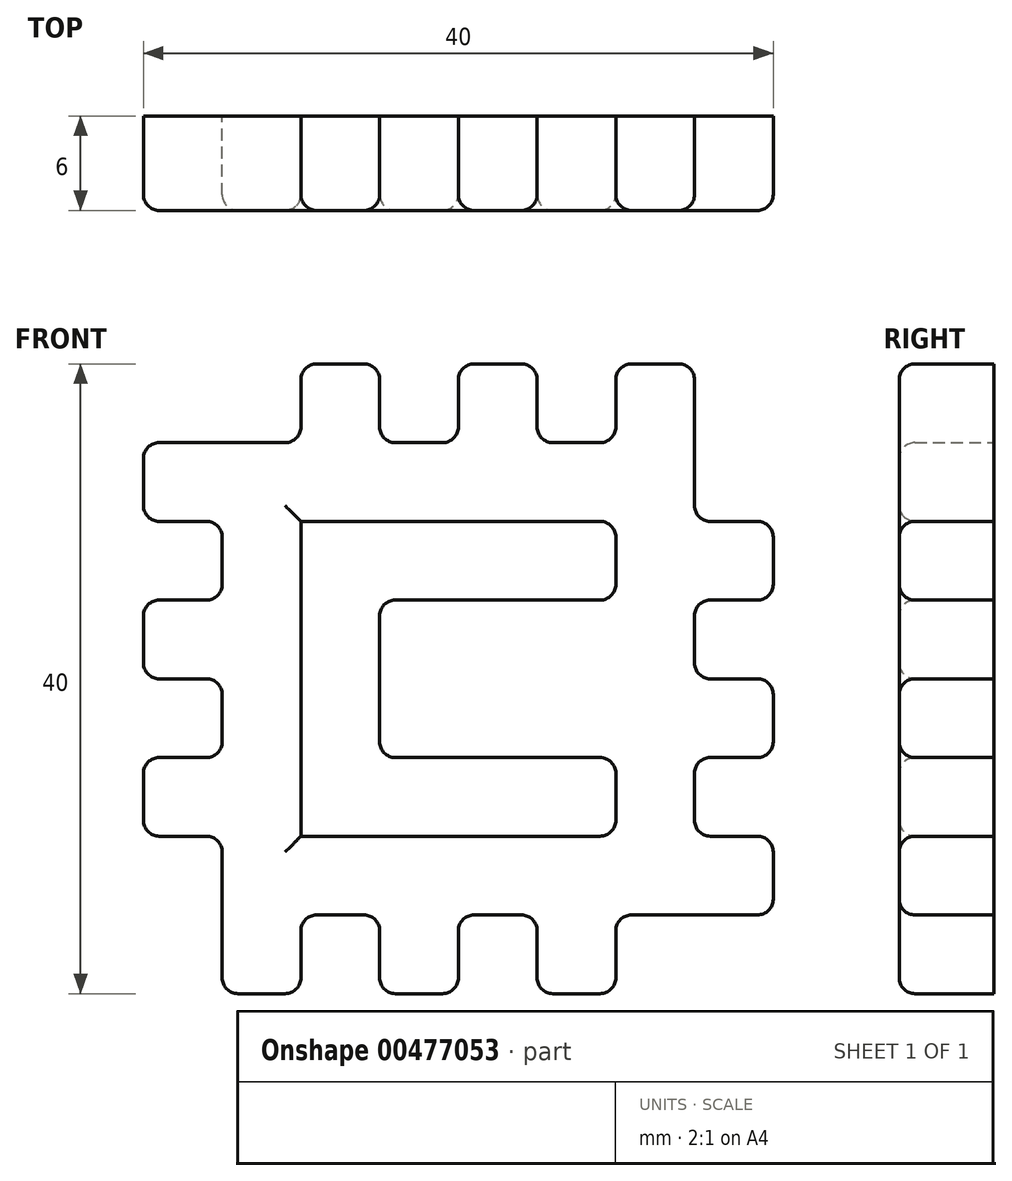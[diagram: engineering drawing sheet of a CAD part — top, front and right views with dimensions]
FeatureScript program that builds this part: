
annotation { "Feature Type Name" : "Feature", "Feature Type Description" : "" }
export const myFeature = defineFeature(function(context is Context, id is Id, definition is map)
    precondition{}
    {
        {
            var Q0;
            Q0=qCreatedBy(makeId("Front.planeOp"),FACE);
            var sketch = newSketch(context, id + "F0", { "sketchPlane" : qUnion([Q0])});
            skLineSegment(sketch, "E0.bottom", {"start": v(-15, -15) * mm, "end": v(15, -15) * mm});
            skLineSegment(sketch, "E0.top", {"start": v(-15, 15) * mm, "end": v(15, 15) * mm});
            skLineSegment(sketch, "E0.left", {"start": v(-15, -15) * mm, "end": v(-15, 15) * mm});
            skLineSegment(sketch, "E0.right", {"start": v(15, -15) * mm, "end": v(15, 15) * mm});
            skPoint(sketch, "E0.middle", {"position": v(0, 0) * mm});
            skLineSegment(sketch, "E1.bottom", {"start": v(-15, 15) * mm, "end": v(-20, 15) * mm});
            skLineSegment(sketch, "E1.top", {"start": v(-15, 10) * mm, "end": v(-20, 10) * mm});
            skLineSegment(sketch, "E1.left", {"start": v(-15, 15) * mm, "end": v(-15, 10) * mm});
            skLineSegment(sketch, "E1.right", {"start": v(-20, 15) * mm, "end": v(-20, 10) * mm});
            skPoint(sketch, "E2", {"position": v(-15, 0) * mm});
            skPoint(sketch, "E3", {"position": v(0, 15) * mm});
            skPoint(sketch, "E4", {"position": v(15, 0) * mm});
            skPoint(sketch, "E5", {"position": v(0, -15) * mm});
            skLineSegment(sketch, "E6.bottom", {"start": v(-15, 0) * mm, "end": v(-20, 0) * mm});
            skLineSegment(sketch, "E6.top", {"start": v(-15, 5) * mm, "end": v(-20, 5) * mm});
            skLineSegment(sketch, "E6.left", {"start": v(-15, 0) * mm, "end": v(-15, 5) * mm});
            skLineSegment(sketch, "E6.right", {"start": v(-20, 0) * mm, "end": v(-20, 5) * mm});
            skPoint(sketch, "E7", {"position": v(-15, -7.74) * mm});
            skPoint(sketch, "E8", {"position": v(-7.28, -15) * mm});
            skPoint(sketch, "E9", {"position": v(7.64, -15) * mm});
            skPoint(sketch, "E10", {"position": v(15, -7.4) * mm});
            skPoint(sketch, "E11", {"position": v(15, 8.08) * mm});
            skPoint(sketch, "E12", {"position": v(7.83, 15) * mm});
            skPoint(sketch, "E13", {"position": v(-7.7, 15) * mm});
            skPoint(sketch, "E14", {"position": v(-15, -5) * mm});
            skPoint(sketch, "E15", {"position": v(-15, -11.17) * mm});
            skPoint(sketch, "E16", {"position": v(-11.04, -15) * mm});
            skPoint(sketch, "E17", {"position": v(-3.27, -15) * mm});
            skPoint(sketch, "E18", {"position": v(5, -15) * mm});
            skPoint(sketch, "E19", {"position": v(11.4, -15) * mm});
            skPoint(sketch, "E20", {"position": v(15, -11.1) * mm});
            skPoint(sketch, "E21", {"position": v(15, -3.78) * mm});
            skPoint(sketch, "E22", {"position": v(15, 3.83) * mm});
            skPoint(sketch, "E23", {"position": v(15, 10) * mm});
            skPoint(sketch, "E24", {"position": v(11.09, 15) * mm});
            skPoint(sketch, "E25", {"position": v(4.04, 15) * mm});
            skPoint(sketch, "E26", {"position": v(-3.6, 15) * mm});
            skPoint(sketch, "E27", {"position": v(-11.54, 15) * mm});
            skLineSegment(sketch, "E28.bottom", {"start": v(-15, -5) * mm, "end": v(-20, -5) * mm});
            skLineSegment(sketch, "E28.top", {"start": v(-15, -10) * mm, "end": v(-20, -10) * mm});
            skLineSegment(sketch, "E28.left", {"start": v(-15, -5) * mm, "end": v(-15, -10) * mm});
            skLineSegment(sketch, "E28.right", {"start": v(-20, -5) * mm, "end": v(-20, -10) * mm});
            skLineSegment(sketch, "E29.bottom", {"start": v(15, 10) * mm, "end": v(20, 10) * mm});
            skLineSegment(sketch, "E29.top", {"start": v(15, 5) * mm, "end": v(20, 5) * mm});
            skLineSegment(sketch, "E29.left", {"start": v(15, 10) * mm, "end": v(15, 5) * mm});
            skLineSegment(sketch, "E29.right", {"start": v(20, 10) * mm, "end": v(20, 5) * mm});
            skLineSegment(sketch, "E30.bottom", {"start": v(15, 0) * mm, "end": v(20, 0) * mm});
            skLineSegment(sketch, "E30.top", {"start": v(15, -5) * mm, "end": v(20, -5) * mm});
            skLineSegment(sketch, "E30.left", {"start": v(15, 0) * mm, "end": v(15, -5) * mm});
            skLineSegment(sketch, "E30.right", {"start": v(20, 0) * mm, "end": v(20, -5) * mm});
            skLineSegment(sketch, "E31.bottom", {"start": v(15, -15) * mm, "end": v(20, -15) * mm});
            skLineSegment(sketch, "E31.top", {"start": v(15, -10) * mm, "end": v(20, -10) * mm});
            skLineSegment(sketch, "E31.left", {"start": v(15, -15) * mm, "end": v(15, -10) * mm});
            skLineSegment(sketch, "E31.right", {"start": v(20, -15) * mm, "end": v(20, -10) * mm});
            skLineSegment(sketch, "E32.bottom", {"start": v(-15, -15) * mm, "end": v(-10, -15) * mm});
            skLineSegment(sketch, "E32.top", {"start": v(-15, -20) * mm, "end": v(-10, -20) * mm});
            skLineSegment(sketch, "E32.left", {"start": v(-15, -15) * mm, "end": v(-15, -20) * mm});
            skLineSegment(sketch, "E32.right", {"start": v(-10, -15) * mm, "end": v(-10, -20) * mm});
            skLineSegment(sketch, "E33.bottom", {"start": v(0, -15) * mm, "end": v(-5, -15) * mm});
            skLineSegment(sketch, "E33.top", {"start": v(0, -20) * mm, "end": v(-5, -20) * mm});
            skLineSegment(sketch, "E33.left", {"start": v(0, -15) * mm, "end": v(0, -20) * mm});
            skLineSegment(sketch, "E33.right", {"start": v(-5, -15) * mm, "end": v(-5, -20) * mm});
            skLineSegment(sketch, "E34.bottom", {"start": v(5, -15) * mm, "end": v(10, -15) * mm});
            skLineSegment(sketch, "E34.top", {"start": v(5, -20) * mm, "end": v(10, -20) * mm});
            skLineSegment(sketch, "E34.left", {"start": v(5, -15) * mm, "end": v(5, -20) * mm});
            skLineSegment(sketch, "E34.right", {"start": v(10, -15) * mm, "end": v(10, -20) * mm});
            skLineSegment(sketch, "E35.bottom", {"start": v(-10, 15) * mm, "end": v(-5, 15) * mm});
            skLineSegment(sketch, "E35.top", {"start": v(-10, 20) * mm, "end": v(-5, 20) * mm});
            skLineSegment(sketch, "E35.left", {"start": v(-10, 15) * mm, "end": v(-10, 20) * mm});
            skLineSegment(sketch, "E35.right", {"start": v(-5, 15) * mm, "end": v(-5, 20) * mm});
            skLineSegment(sketch, "E36.bottom", {"start": v(0, 15) * mm, "end": v(5, 15) * mm});
            skLineSegment(sketch, "E36.top", {"start": v(0, 20) * mm, "end": v(5, 20) * mm});
            skLineSegment(sketch, "E36.left", {"start": v(0, 15) * mm, "end": v(0, 20) * mm});
            skLineSegment(sketch, "E36.right", {"start": v(5, 15) * mm, "end": v(5, 20) * mm});
            skLineSegment(sketch, "E37.bottom", {"start": v(15, 15) * mm, "end": v(10, 15) * mm});
            skLineSegment(sketch, "E37.top", {"start": v(15, 20) * mm, "end": v(10, 20) * mm});
            skLineSegment(sketch, "E37.left", {"start": v(15, 15) * mm, "end": v(15, 20) * mm});
            skLineSegment(sketch, "E37.right", {"start": v(10, 15) * mm, "end": v(10, 20) * mm});
            skLineSegment(sketch, "E38.bottom", {"start": v(10, 10) * mm, "end": v(-10, 10) * mm});
            skLineSegment(sketch, "E38.top", {"start": v(10, 5) * mm, "end": v(-10, 5) * mm});
            skLineSegment(sketch, "E38.left", {"start": v(10, 10) * mm, "end": v(10, 5) * mm});
            skLineSegment(sketch, "E38.right", {"start": v(-10, 10) * mm, "end": v(-10, 5) * mm});
            skLineSegment(sketch, "E39.bottom", {"start": v(10, -5) * mm, "end": v(-10, -5) * mm});
            skLineSegment(sketch, "E39.top", {"start": v(10, -10) * mm, "end": v(-10, -10) * mm});
            skLineSegment(sketch, "E39.left", {"start": v(10, -5) * mm, "end": v(10, -10) * mm});
            skLineSegment(sketch, "E39.right", {"start": v(-10, -5) * mm, "end": v(-10, -10) * mm});
            skLineSegment(sketch, "E40.bottom", {"start": v(-5, 10) * mm, "end": v(-10, 10) * mm});
            skLineSegment(sketch, "E40.top", {"start": v(-5, -10) * mm, "end": v(-10, -10) * mm});
            skLineSegment(sketch, "E40.left", {"start": v(-5, 10) * mm, "end": v(-5, -10) * mm});
            skLineSegment(sketch, "E40.right", {"start": v(-10, 10) * mm, "end": v(-10, -10) * mm});
            skSolve(sketch);
        }
        {
            var Q0;
            Q0 = qSketchRegion(id + "F0", true);
            extrude(context, id + "F1", {"entities" : qUnion([Q0]), "depth" : 6 * mm});
        }
        {
            var Q0;
            Q0=makeQuery(id+"F1.opExtrude","SWEPT_EDGE",EDGE,{"disambiguationData":[OSD([sQuery(id+"F0.wireOp",EDGE,"E40.bottom"),sQuery(id+"F0.wireOp",EDGE,"E40.right")])]});
            var Q1;
            Q1=makeQuery(id+"F1.opExtrude","SWEPT_EDGE",EDGE,{"disambiguationData":[OSD([sQuery(id+"F0.wireOp",EDGE,"E39.bottom"),sQuery(id+"F0.wireOp",EDGE,"E40.left")])]});
            var Q2;
            Q2=makeQuery(id+"F1.opExtrude","SWEPT_EDGE",EDGE,{"disambiguationData":[OSD([sQuery(id+"F0.wireOp",EDGE,"E38.bottom"),sQuery(id+"F0.wireOp",EDGE,"E38.left")])]});
            var Q3;
            Q3=makeQuery(id+"F1.opExtrude","SWEPT_EDGE",EDGE,{"disambiguationData":[OSD([sQuery(id+"F0.wireOp",EDGE,"E39.bottom"),sQuery(id+"F0.wireOp",EDGE,"E39.left")])]});
            var Q4;
            Q4=makeQuery(id+"F1.opExtrude","SWEPT_EDGE",EDGE,{"disambiguationData":[OSD([sQuery(id+"F0.wireOp",EDGE,"E38.top"),sQuery(id+"F0.wireOp",EDGE,"E38.left")])]});
            var Q5;
            Q5=makeQuery(id+"F1.opExtrude","SWEPT_EDGE",EDGE,{"disambiguationData":[OSD([sQuery(id+"F0.wireOp",EDGE,"E39.top"),sQuery(id+"F0.wireOp",EDGE,"E39.left")])]});
            var Q6;
            Q6=makeQuery(id+"F1.opExtrude","SWEPT_EDGE",EDGE,{"disambiguationData":[OSD([sQuery(id+"F0.wireOp",EDGE,"E38.top"),sQuery(id+"F0.wireOp",EDGE,"E40.left")])]});
            var Q7;
            Q7=makeQuery(id+"F1.opExtrude","SWEPT_EDGE",EDGE,{"disambiguationData":[OSD([sQuery(id+"F0.wireOp",EDGE,"E40.top"),sQuery(id+"F0.wireOp",EDGE,"E40.right")])]});
            var Q8;
            Q8=makeQuery(id+"F1.opExtrude","CAP_EDGE",EDGE,{"disambiguationData":[OSD([sQuery(id+"F0.wireOp",EDGE,"E39.bottom")])],"isStart":false});
            var Q9;
            Q9=makeQuery(id+"F1.opExtrude","CAP_EDGE",EDGE,{"disambiguationData":[OSD([sQuery(id+"F0.wireOp",EDGE,"E40.left")])],"isStart":false});
            fillet(context, id + "F2", {"entities" : qUnion([Q0, Q1, Q2, Q3, Q4, Q5, Q6, Q7, Q8, Q9]), "radius" : 1 * mm, "tangentPropagation" : true, "allowEdgeOverflow" : false});
        }
        {
            var Q0;
            Q0=makeQuery(id+"F1.opExtrude","CAP_EDGE",EDGE,{"disambiguationData":[OSD([sQuery(id+"F0.wireOp",EDGE,"E35.right")])],"isStart":false});
            var Q1;
            {var subQ0=sQuery(id+"F0.wireOp",EDGE,"E0.top");Q1=makeQuery(id+"F1.opExtrude","CAP_EDGE",EDGE,{"disambiguationData":[OSD([subQ0]),TDD([makeQuery(id+"F0.imprint","IMPRINT",EDGE,{"disambiguationData":[TD([[makeQuery(id+"F0.imprint","INTERSECT",VERTEX,{"derivedFrom":[subQ0,sQuery(id+"F0.wireOp",EDGE,"E35.bottom"),sQuery(id+"F0.wireOp",EDGE,"E35.right")]}),-1.0]])],"derivedFrom":subQ0})])],"isStart":false});}
            var Q2;
            {var subQ0=sQuery(id+"F0.wireOp",EDGE,"E0.top");Q2=makeQuery(id+"F1.opExtrude","CAP_EDGE",EDGE,{"disambiguationData":[OSD([subQ0]),TDD([makeQuery(id+"F0.imprint","IMPRINT",EDGE,{"disambiguationData":[TD([[makeQuery(id+"F0.imprint","INTERSECT",VERTEX,{"derivedFrom":[subQ0,sQuery(id+"F0.wireOp",EDGE,"E37.bottom"),sQuery(id+"F0.wireOp",EDGE,"E37.right")]}),1.0]])],"derivedFrom":subQ0})])],"isStart":false});}
            var Q3;
            Q3=makeQuery(id+"F1.opExtrude","CAP_EDGE",EDGE,{"disambiguationData":[OSD([sQuery(id+"F0.wireOp",EDGE,"E36.right")])],"isStart":false});
            var Q4;
            Q4=makeQuery(id+"F1.opExtrude","SWEPT_EDGE",EDGE,{"disambiguationData":[OSD([sQuery(id+"F0.wireOp",EDGE,"E0.top"),sQuery(id+"F0.wireOp",EDGE,"E37.bottom"),sQuery(id+"F0.wireOp",EDGE,"E37.right")])]});
            var Q5;
            Q5=makeQuery(id+"F1.opExtrude","SWEPT_EDGE",EDGE,{"disambiguationData":[OSD([sQuery(id+"F0.wireOp",EDGE,"E0.top"),sQuery(id+"F0.wireOp",EDGE,"E36.bottom"),sQuery(id+"F0.wireOp",EDGE,"E36.left")])]});
            var Q6;
            Q6=makeQuery(id+"F1.opExtrude","CAP_EDGE",EDGE,{"disambiguationData":[OSD([sQuery(id+"F0.wireOp",EDGE,"E0.top"),sQuery(id+"F0.wireOp",EDGE,"E1.bottom")])],"isStart":false});
            var Q7;
            Q7=makeQuery(id+"F1.opExtrude","SWEPT_EDGE",EDGE,{"disambiguationData":[OSD([sQuery(id+"F0.wireOp",EDGE,"E0.top"),sQuery(id+"F0.wireOp",EDGE,"E35.bottom"),sQuery(id+"F0.wireOp",EDGE,"E35.left")])]});
            var Q8;
            Q8=makeQuery(id+"F1.opExtrude","CAP_EDGE",EDGE,{"disambiguationData":[OSD([sQuery(id+"F0.wireOp",EDGE,"E35.top")])],"isStart":false});
            var Q9;
            Q9=makeQuery(id+"F1.opExtrude","SWEPT_EDGE",EDGE,{"disambiguationData":[OSD([sQuery(id+"F0.wireOp",EDGE,"E35.top"),sQuery(id+"F0.wireOp",EDGE,"E35.left")])]});
            var Q10;
            {var subQ0=sQuery(id+"F0.wireOp",EDGE,"E0.left");Q10=makeQuery(id+"F1.opExtrude","CAP_EDGE",EDGE,{"disambiguationData":[OSD([subQ0]),TDD([makeQuery(id+"F0.imprint","IMPRINT",EDGE,{"disambiguationData":[TD([[makeQuery(id+"F0.imprint","INTERSECT",VERTEX,{"derivedFrom":[subQ0,sQuery(id+"F0.wireOp",EDGE,"E1.top"),sQuery(id+"F0.wireOp",EDGE,"E1.left")]}),1.0]])],"derivedFrom":subQ0})])],"isStart":false});}
            var Q11;
            Q11=makeQuery(id+"F1.opExtrude","SWEPT_EDGE",EDGE,{"disambiguationData":[OSD([sQuery(id+"F0.wireOp",EDGE,"E0.top"),sQuery(id+"F0.wireOp",EDGE,"E35.bottom"),sQuery(id+"F0.wireOp",EDGE,"E35.right")])]});
            var Q12;
            Q12=makeQuery(id+"F1.opExtrude","SWEPT_EDGE",EDGE,{"disambiguationData":[OSD([sQuery(id+"F0.wireOp",EDGE,"E0.top"),sQuery(id+"F0.wireOp",EDGE,"E36.bottom"),sQuery(id+"F0.wireOp",EDGE,"E36.right")])]});
            var Q13;
            Q13=makeQuery(id+"F1.opExtrude","SWEPT_EDGE",EDGE,{"disambiguationData":[OSD([sQuery(id+"F0.wireOp",EDGE,"E36.top"),sQuery(id+"F0.wireOp",EDGE,"E36.right")])]});
            var Q14;
            Q14=makeQuery(id+"F1.opExtrude","SWEPT_EDGE",EDGE,{"disambiguationData":[OSD([sQuery(id+"F0.wireOp",EDGE,"E35.top"),sQuery(id+"F0.wireOp",EDGE,"E35.right")])]});
            var Q15;
            Q15=makeQuery(id+"F1.opExtrude","SWEPT_EDGE",EDGE,{"disambiguationData":[OSD([sQuery(id+"F0.wireOp",EDGE,"E36.top"),sQuery(id+"F0.wireOp",EDGE,"E36.left")])]});
            var Q16;
            Q16=makeQuery(id+"F1.opExtrude","SWEPT_EDGE",EDGE,{"disambiguationData":[OSD([sQuery(id+"F0.wireOp",EDGE,"E37.top"),sQuery(id+"F0.wireOp",EDGE,"E37.right")])]});
            var Q17;
            Q17=makeQuery(id+"F1.opExtrude","SWEPT_EDGE",EDGE,{"disambiguationData":[OSD([sQuery(id+"F0.wireOp",EDGE,"E1.bottom"),sQuery(id+"F0.wireOp",EDGE,"E1.right")])]});
            var Q18;
            Q18=makeQuery(id+"F1.opExtrude","CAP_EDGE",EDGE,{"disambiguationData":[OSD([sQuery(id+"F0.wireOp",EDGE,"E1.right")])],"isStart":false});
            var Q19;
            Q19=makeQuery(id+"F1.opExtrude","SWEPT_EDGE",EDGE,{"disambiguationData":[OSD([sQuery(id+"F0.wireOp",EDGE,"E1.top"),sQuery(id+"F0.wireOp",EDGE,"E1.right")])]});
            var Q20;
            Q20=makeQuery(id+"F1.opExtrude","CAP_FACE",FACE,{"disambiguationData":[OSD([sQuery(id+"F0.wireOp",EDGE,"E0.bottom"),sQuery(id+"F0.wireOp",EDGE,"E0.top"),sQuery(id+"F0.wireOp",EDGE,"E0.left"),sQuery(id+"F0.wireOp",EDGE,"E0.right"),sQuery(id+"F0.wireOp",EDGE,"E1.bottom"),sQuery(id+"F0.wireOp",EDGE,"E1.top"),sQuery(id+"F0.wireOp",EDGE,"E1.right"),sQuery(id+"F0.wireOp",EDGE,"E6.bottom"),sQuery(id+"F0.wireOp",EDGE,"E6.top"),sQuery(id+"F0.wireOp",EDGE,"E6.right"),sQuery(id+"F0.wireOp",EDGE,"E28.bottom"),sQuery(id+"F0.wireOp",EDGE,"E28.top"),sQuery(id+"F0.wireOp",EDGE,"E28.right"),sQuery(id+"F0.wireOp",EDGE,"E29.bottom"),sQuery(id+"F0.wireOp",EDGE,"E29.top"),sQuery(id+"F0.wireOp",EDGE,"E29.right"),sQuery(id+"F0.wireOp",EDGE,"E30.bottom"),sQuery(id+"F0.wireOp",EDGE,"E30.top"),sQuery(id+"F0.wireOp",EDGE,"E30.right"),sQuery(id+"F0.wireOp",EDGE,"E31.bottom"),sQuery(id+"F0.wireOp",EDGE,"E31.top"),sQuery(id+"F0.wireOp",EDGE,"E31.right"),sQuery(id+"F0.wireOp",EDGE,"E32.top"),sQuery(id+"F0.wireOp",EDGE,"E32.left"),sQuery(id+"F0.wireOp",EDGE,"E32.right"),sQuery(id+"F0.wireOp",EDGE,"E33.top"),sQuery(id+"F0.wireOp",EDGE,"E33.left"),sQuery(id+"F0.wireOp",EDGE,"E33.right"),sQuery(id+"F0.wireOp",EDGE,"E34.top"),sQuery(id+"F0.wireOp",EDGE,"E34.left"),sQuery(id+"F0.wireOp",EDGE,"E34.right"),sQuery(id+"F0.wireOp",EDGE,"E35.top"),sQuery(id+"F0.wireOp",EDGE,"E35.left"),sQuery(id+"F0.wireOp",EDGE,"E35.right"),sQuery(id+"F0.wireOp",EDGE,"E36.top"),sQuery(id+"F0.wireOp",EDGE,"E36.left"),sQuery(id+"F0.wireOp",EDGE,"E36.right"),sQuery(id+"F0.wireOp",EDGE,"E37.top"),sQuery(id+"F0.wireOp",EDGE,"E37.left"),sQuery(id+"F0.wireOp",EDGE,"E37.right"),sQuery(id+"F0.wireOp",EDGE,"E38.bottom"),sQuery(id+"F0.wireOp",EDGE,"E38.top"),sQuery(id+"F0.wireOp",EDGE,"E38.left"),sQuery(id+"F0.wireOp",EDGE,"E39.bottom"),sQuery(id+"F0.wireOp",EDGE,"E39.top"),sQuery(id+"F0.wireOp",EDGE,"E39.left"),sQuery(id+"F0.wireOp",EDGE,"E40.bottom"),sQuery(id+"F0.wireOp",EDGE,"E40.top"),sQuery(id+"F0.wireOp",EDGE,"E40.left"),sQuery(id+"F0.wireOp",EDGE,"E40.right")])],"isStart":false});
            var Q21;
            Q21=makeQuery(id+"F1.opExtrude","SWEPT_EDGE",EDGE,{"disambiguationData":[OSD([sQuery(id+"F0.wireOp",EDGE,"E0.left"),sQuery(id+"F0.wireOp",EDGE,"E6.top"),sQuery(id+"F0.wireOp",EDGE,"E6.left")])]});
            var Q22;
            Q22=makeQuery(id+"F1.opExtrude","SWEPT_EDGE",EDGE,{"disambiguationData":[OSD([sQuery(id+"F0.wireOp",EDGE,"E6.top"),sQuery(id+"F0.wireOp",EDGE,"E6.right")])]});
            var Q23;
            Q23=makeQuery(id+"F1.opExtrude","SWEPT_EDGE",EDGE,{"disambiguationData":[OSD([sQuery(id+"F0.wireOp",EDGE,"E6.bottom"),sQuery(id+"F0.wireOp",EDGE,"E6.right")])]});
            var Q24;
            Q24=makeQuery(id+"F1.opExtrude","SWEPT_EDGE",EDGE,{"disambiguationData":[OSD([sQuery(id+"F0.wireOp",EDGE,"E0.left"),sQuery(id+"F0.wireOp",EDGE,"E28.bottom"),sQuery(id+"F0.wireOp",EDGE,"E28.left")])]});
            var Q25;
            Q25=makeQuery(id+"F1.opExtrude","SWEPT_EDGE",EDGE,{"disambiguationData":[OSD([sQuery(id+"F0.wireOp",EDGE,"E28.bottom"),sQuery(id+"F0.wireOp",EDGE,"E28.right")])]});
            var Q26;
            Q26=makeQuery(id+"F1.opExtrude","SWEPT_EDGE",EDGE,{"disambiguationData":[OSD([sQuery(id+"F0.wireOp",EDGE,"E0.left"),sQuery(id+"F0.wireOp",EDGE,"E6.bottom"),sQuery(id+"F0.wireOp",EDGE,"E6.left")])]});
            var Q27;
            Q27=makeQuery(id+"F1.opExtrude","SWEPT_EDGE",EDGE,{"disambiguationData":[OSD([sQuery(id+"F0.wireOp",EDGE,"E0.left"),sQuery(id+"F0.wireOp",EDGE,"E1.top"),sQuery(id+"F0.wireOp",EDGE,"E1.left")])]});
            var Q28;
            Q28=makeQuery(id+"F1.opExtrude","SWEPT_EDGE",EDGE,{"disambiguationData":[OSD([sQuery(id+"F0.wireOp",EDGE,"E28.top"),sQuery(id+"F0.wireOp",EDGE,"E28.right")])]});
            var Q29;
            Q29=makeQuery(id+"F1.opExtrude","SWEPT_EDGE",EDGE,{"disambiguationData":[OSD([sQuery(id+"F0.wireOp",EDGE,"E0.left"),sQuery(id+"F0.wireOp",EDGE,"E28.top"),sQuery(id+"F0.wireOp",EDGE,"E28.left")])]});
            var Q30;
            Q30=makeQuery(id+"F1.opExtrude","SWEPT_EDGE",EDGE,{"disambiguationData":[OSD([sQuery(id+"F0.wireOp",EDGE,"E32.top"),sQuery(id+"F0.wireOp",EDGE,"E32.left")])]});
            var Q31;
            Q31=makeQuery(id+"F1.opExtrude","SWEPT_EDGE",EDGE,{"disambiguationData":[OSD([sQuery(id+"F0.wireOp",EDGE,"E0.bottom"),sQuery(id+"F0.wireOp",EDGE,"E33.bottom"),sQuery(id+"F0.wireOp",EDGE,"E33.right")])]});
            var Q32;
            Q32=makeQuery(id+"F1.opExtrude","SWEPT_EDGE",EDGE,{"disambiguationData":[OSD([sQuery(id+"F0.wireOp",EDGE,"E0.bottom"),sQuery(id+"F0.wireOp",EDGE,"E34.bottom"),sQuery(id+"F0.wireOp",EDGE,"E34.left")])]});
            var Q33;
            Q33=makeQuery(id+"F1.opExtrude","SWEPT_EDGE",EDGE,{"disambiguationData":[OSD([sQuery(id+"F0.wireOp",EDGE,"E31.bottom"),sQuery(id+"F0.wireOp",EDGE,"E31.right")])]});
            var Q34;
            Q34=makeQuery(id+"F1.opExtrude","SWEPT_EDGE",EDGE,{"disambiguationData":[OSD([sQuery(id+"F0.wireOp",EDGE,"E34.top"),sQuery(id+"F0.wireOp",EDGE,"E34.right")])]});
            var Q35;
            Q35=makeQuery(id+"F1.opExtrude","SWEPT_EDGE",EDGE,{"disambiguationData":[OSD([sQuery(id+"F0.wireOp",EDGE,"E34.top"),sQuery(id+"F0.wireOp",EDGE,"E34.left")])]});
            var Q36;
            Q36=makeQuery(id+"F1.opExtrude","SWEPT_EDGE",EDGE,{"disambiguationData":[OSD([sQuery(id+"F0.wireOp",EDGE,"E33.top"),sQuery(id+"F0.wireOp",EDGE,"E33.left")])]});
            var Q37;
            Q37=makeQuery(id+"F1.opExtrude","SWEPT_EDGE",EDGE,{"disambiguationData":[OSD([sQuery(id+"F0.wireOp",EDGE,"E33.top"),sQuery(id+"F0.wireOp",EDGE,"E33.right")])]});
            var Q38;
            Q38=makeQuery(id+"F1.opExtrude","SWEPT_EDGE",EDGE,{"disambiguationData":[OSD([sQuery(id+"F0.wireOp",EDGE,"E32.top"),sQuery(id+"F0.wireOp",EDGE,"E32.right")])]});
            var Q39;
            Q39=makeQuery(id+"F1.opExtrude","SWEPT_EDGE",EDGE,{"disambiguationData":[OSD([sQuery(id+"F0.wireOp",EDGE,"E0.bottom"),sQuery(id+"F0.wireOp",EDGE,"E32.bottom"),sQuery(id+"F0.wireOp",EDGE,"E32.right")])]});
            var Q40;
            Q40=makeQuery(id+"F1.opExtrude","SWEPT_EDGE",EDGE,{"disambiguationData":[OSD([sQuery(id+"F0.wireOp",EDGE,"E0.bottom"),sQuery(id+"F0.wireOp",EDGE,"E33.bottom"),sQuery(id+"F0.wireOp",EDGE,"E33.left")])]});
            var Q41;
            Q41=makeQuery(id+"F1.opExtrude","SWEPT_EDGE",EDGE,{"disambiguationData":[OSD([sQuery(id+"F0.wireOp",EDGE,"E0.bottom"),sQuery(id+"F0.wireOp",EDGE,"E34.bottom"),sQuery(id+"F0.wireOp",EDGE,"E34.right")])]});
            var Q42;
            Q42=makeQuery(id+"F1.opExtrude","SWEPT_EDGE",EDGE,{"disambiguationData":[OSD([sQuery(id+"F0.wireOp",EDGE,"E31.top"),sQuery(id+"F0.wireOp",EDGE,"E31.right")])]});
            var Q43;
            Q43=makeQuery(id+"F1.opExtrude","SWEPT_EDGE",EDGE,{"disambiguationData":[OSD([sQuery(id+"F0.wireOp",EDGE,"E0.right"),sQuery(id+"F0.wireOp",EDGE,"E31.top"),sQuery(id+"F0.wireOp",EDGE,"E31.left")])]});
            var Q44;
            Q44=makeQuery(id+"F1.opExtrude","SWEPT_EDGE",EDGE,{"disambiguationData":[OSD([sQuery(id+"F0.wireOp",EDGE,"E29.bottom"),sQuery(id+"F0.wireOp",EDGE,"E29.right")])]});
            var Q45;
            Q45=makeQuery(id+"F1.opExtrude","SWEPT_EDGE",EDGE,{"disambiguationData":[OSD([sQuery(id+"F0.wireOp",EDGE,"E37.top"),sQuery(id+"F0.wireOp",EDGE,"E37.left")])]});
            var Q46;
            Q46=makeQuery(id+"F1.opExtrude","SWEPT_EDGE",EDGE,{"disambiguationData":[OSD([sQuery(id+"F0.wireOp",EDGE,"E0.right"),sQuery(id+"F0.wireOp",EDGE,"E30.top"),sQuery(id+"F0.wireOp",EDGE,"E30.left")])]});
            var Q47;
            Q47=makeQuery(id+"F1.opExtrude","SWEPT_EDGE",EDGE,{"disambiguationData":[OSD([sQuery(id+"F0.wireOp",EDGE,"E30.top"),sQuery(id+"F0.wireOp",EDGE,"E30.right")])]});
            var Q48;
            Q48=makeQuery(id+"F1.opExtrude","SWEPT_EDGE",EDGE,{"disambiguationData":[OSD([sQuery(id+"F0.wireOp",EDGE,"E0.right"),sQuery(id+"F0.wireOp",EDGE,"E29.bottom"),sQuery(id+"F0.wireOp",EDGE,"E29.left")])]});
            var Q49;
            Q49=makeQuery(id+"F1.opExtrude","SWEPT_EDGE",EDGE,{"disambiguationData":[OSD([sQuery(id+"F0.wireOp",EDGE,"E0.right"),sQuery(id+"F0.wireOp",EDGE,"E29.top"),sQuery(id+"F0.wireOp",EDGE,"E29.left")])]});
            var Q50;
            Q50=makeQuery(id+"F1.opExtrude","SWEPT_EDGE",EDGE,{"disambiguationData":[OSD([sQuery(id+"F0.wireOp",EDGE,"E0.right"),sQuery(id+"F0.wireOp",EDGE,"E30.bottom"),sQuery(id+"F0.wireOp",EDGE,"E30.left")])]});
            var Q51;
            Q51=makeQuery(id+"F1.opExtrude","SWEPT_EDGE",EDGE,{"disambiguationData":[OSD([sQuery(id+"F0.wireOp",EDGE,"E30.bottom"),sQuery(id+"F0.wireOp",EDGE,"E30.right")])]});
            var Q52;
            Q52=makeQuery(id+"F1.opExtrude","SWEPT_EDGE",EDGE,{"disambiguationData":[OSD([sQuery(id+"F0.wireOp",EDGE,"E29.top"),sQuery(id+"F0.wireOp",EDGE,"E29.right")])]});
            fillet(context, id + "F3", {"entities" : qUnion([Q0, Q1, Q2, Q3, Q4, Q5, Q6, Q7, Q8, Q9, Q10, Q11, Q12, Q13, Q14, Q15, Q16, Q17, Q18, Q19, Q20, Q21, Q22, Q23, Q24, Q25, Q26, Q27, Q28, Q29, Q30, Q31, Q32, Q33, Q34, Q35, Q36, Q37, Q38, Q39, Q40, Q41, Q42, Q43, Q44, Q45, Q46, Q47, Q48, Q49, Q50, Q51, Q52]), "radius" : 1 * mm, "tangentPropagation" : true, "allowEdgeOverflow" : false});
        }
    });
